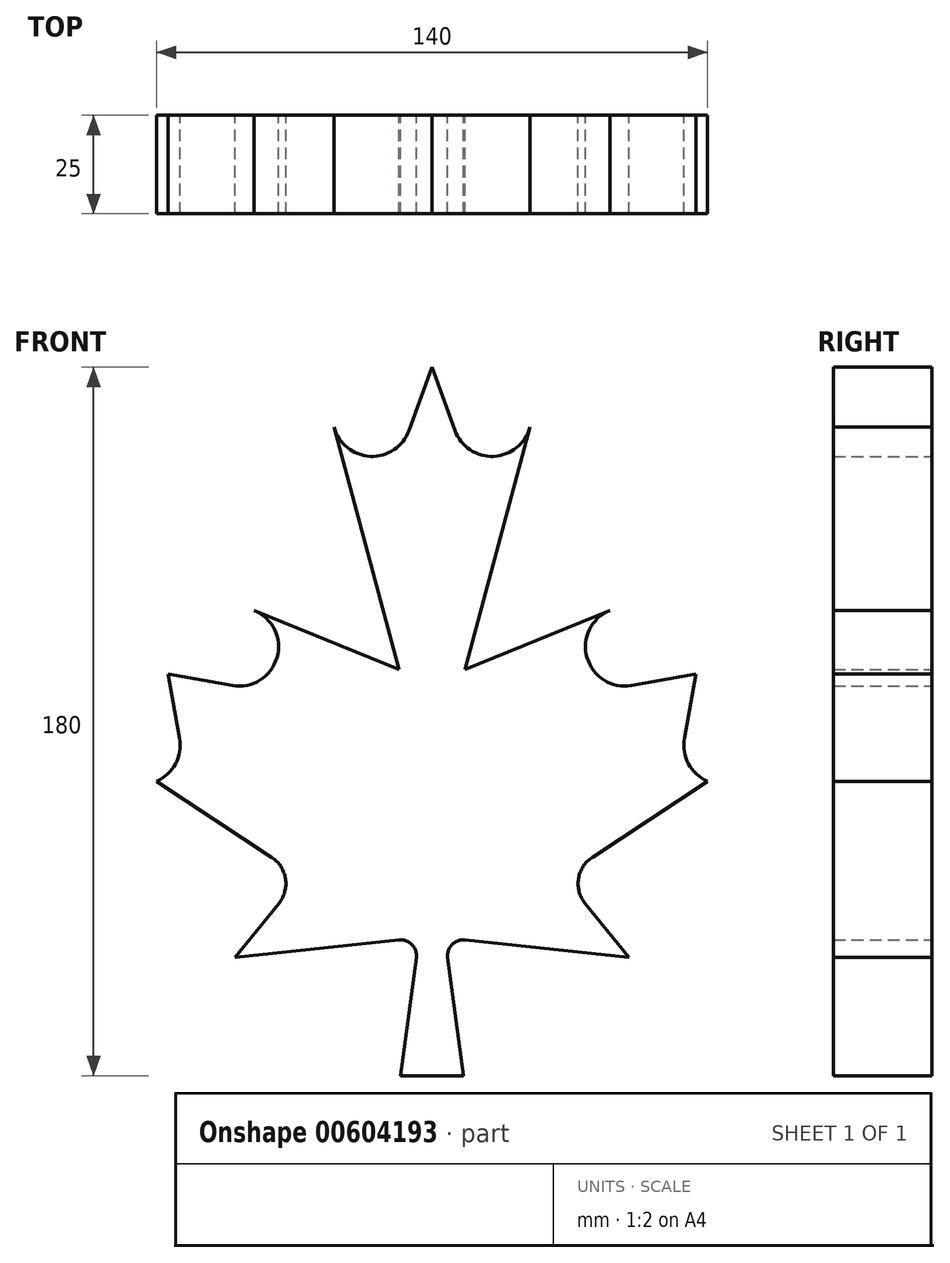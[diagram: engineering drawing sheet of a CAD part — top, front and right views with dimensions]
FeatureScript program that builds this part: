
annotation { "Feature Type Name" : "Feature", "Feature Type Description" : "" }
export const myFeature = defineFeature(function(context is Context, id is Id, definition is map)
    precondition{}
    {
        {
            var Q0;
            Q0=qCreatedBy(makeId("Front.planeOp"),FACE);
            var sketch = newSketch(context, id + "F0", { "sketchPlane" : qUnion([Q0])});
            skLineSegment(sketch, "E0", {"start": v(0, 0) * mm, "end": v(16, 0) * mm});
            skLineSegment(sketch, "E1", {"start": v(16, 0) * mm, "end": v(12, 30) * mm});
            skLineSegment(sketch, "E2", {"start": v(0, 0) * mm, "end": v(4, 30) * mm});
            skPoint(sketch, "E3", {"position": v(8, 0) * mm});
            skLineSegment(sketch, "E4", {"start": v(58, 30) * mm, "end": v(16.4, 34.5) * mm});
            skArc(sketch, "E5", {"start": v(16.4, 34.5) * mm, "mid": v(13.1, 33.32) * mm, "end": v(12, 30) * mm});
            skLineSegment(sketch, "E6", {"start": v(58, 30) * mm, "end": v(46.9, 43.8) * mm});
            skLineSegment(sketch, "E7", {"start": v(78, 74.81) * mm, "end": v(48.72, 55.5) * mm});
            skArc(sketch, "E8", {"start": v(48.72, 55.5) * mm, "mid": v(45.22, 50.05) * mm, "end": v(46.9, 43.8) * mm});
            skLineSegment(sketch, "E9", {"start": v(75, 102) * mm, "end": v(72.13, 85.73) * mm});
            skArc(sketch, "E10", {"start": v(72.13, 85.73) * mm, "mid": v(73.17, 79.25) * mm, "end": v(78, 74.81) * mm});
            skLineSegment(sketch, "E11", {"start": v(75, 102) * mm, "end": v(58.73, 99.13) * mm});
            skArc(sketch, "E12", {"start": v(53.2, 118.23) * mm, "mid": v(47.39, 106.2) * mm, "end": v(58.73, 99.13) * mm});
            skLineSegment(sketch, "E13", {"start": v(53.2, 118.23) * mm, "end": v(16.4, 103.14) * mm});
            skLineSegment(sketch, "E14", {"start": v(16.4, 103.14) * mm, "end": v(32.9, 164.76) * mm});
            skLineSegment(sketch, "E15", {"start": v(8, 180) * mm, "end": v(13.85, 163.93) * mm});
            skPoint(sketch, "E15.endSnap0", {"position": v(13.1, 33.32) * mm});
            skLineSegment(sketch, "E16", {"start": v(8, 180) * mm, "end": v(2.15, 163.93) * mm});
            skArc(sketch, "E17", {"start": v(13.85, 163.93) * mm, "mid": v(23.68, 157.36) * mm, "end": v(32.9, 164.76) * mm});
            skLineSegment(sketch, "E18", {"start": v(8, 180) * mm, "end": v(8, 93.67) * mm, "construction": true});
            skLineSegment(sketch, "E19", {"start": v(58.73, 99.13) * mm, "end": v(72.13, 85.73) * mm, "construction": true});
            skPoint(sketch, "E20", {"position": v(65.43, 92.43) * mm});
            skLineSegment(sketch, "E21", {"start": v(75, 102) * mm, "end": v(33.48, 60.48) * mm, "construction": true});
            skLineSegment(sketch, "E22", {"start": v(-42, 30) * mm, "end": v(-0.4, 34.5) * mm});
            skArc(sketch, "E23", {"start": v(4, 30) * mm, "mid": v(2.9, 33.32) * mm, "end": v(-0.4, 34.5) * mm});
            skLineSegment(sketch, "E24", {"start": v(-42, 30) * mm, "end": v(-30.9, 43.8) * mm});
            skLineSegment(sketch, "E25", {"start": v(-62, 74.81) * mm, "end": v(-32.72, 55.5) * mm});
            skArc(sketch, "E26", {"start": v(-30.9, 43.8) * mm, "mid": v(-29.22, 50.05) * mm, "end": v(-32.72, 55.5) * mm});
            skLineSegment(sketch, "E27", {"start": v(-59, 102) * mm, "end": v(-56.13, 85.73) * mm});
            skLineSegment(sketch, "E28", {"start": v(-59, 102) * mm, "end": v(-42.73, 99.13) * mm});
            skArc(sketch, "E29", {"start": v(-62, 74.81) * mm, "mid": v(-57.17, 79.25) * mm, "end": v(-56.13, 85.73) * mm});
            skLineSegment(sketch, "E30", {"start": v(-56.13, 85.73) * mm, "end": v(-42.73, 99.13) * mm, "construction": true});
            skPoint(sketch, "E31", {"position": v(-49.43, 92.43) * mm});
            skLineSegment(sketch, "E32", {"start": v(-59, 102) * mm, "end": v(-49.43, 92.43) * mm, "construction": true});
            skLineSegment(sketch, "E33", {"start": v(-49.43, 92.43) * mm, "end": v(-21.57, 64.57) * mm, "construction": true});
            skLineSegment(sketch, "E34", {"start": v(-16.9, 164.76) * mm, "end": v(-0.4, 103.14) * mm});
            skArc(sketch, "E35", {"start": v(-16.9, 164.76) * mm, "mid": v(-7.68, 157.36) * mm, "end": v(2.15, 163.93) * mm});
            skLineSegment(sketch, "E36", {"start": v(-0.4, 103.14) * mm, "end": v(-37.2, 118.23) * mm});
            skArc(sketch, "E37", {"start": v(-42.73, 99.13) * mm, "mid": v(-31.39, 106.2) * mm, "end": v(-37.2, 118.23) * mm});
            skSolve(sketch);
        }
        {
            var Q0;
            Q0 = qSketchRegion(id + "F0", true);
            extrude(context, id + "F1", {"entities" : qUnion([Q0]), "depth" : 25 * mm, "offsetDistance" : 25 * mm});
        }
    });
